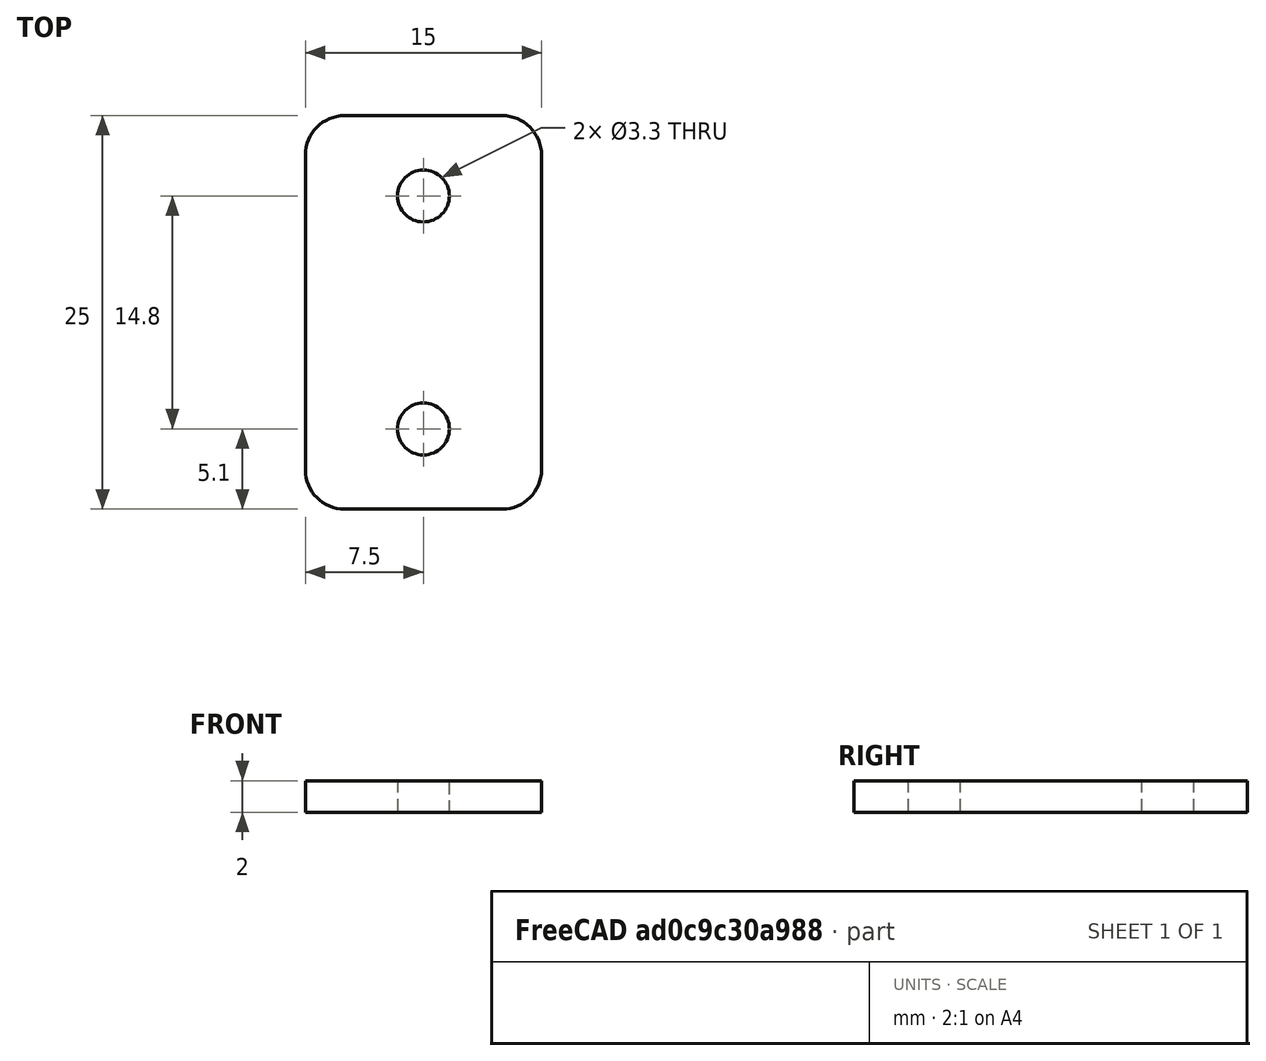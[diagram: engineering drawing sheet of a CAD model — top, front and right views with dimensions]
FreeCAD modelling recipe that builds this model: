
FCSTD DOCUMENT  (FreeCAD 1.0R39109 (Git))
Label: joint_screen
License: All rights reserved
LicenseURL: https://en.wikipedia.org/wiki/All_rights_reserved
objects: Sketcher::SketchObject×1, PartDesign::Pad×1, PartDesign::Body×1
note: 6 computed .brp shape members not serialized (recipe doc carries the construction recipe); baked Part::Feature solids carry a one-line shape summary decoded from their .brp

FEATURE [Sketcher::SketchObject] Sketch
  ArcFitTolerance = 1e-06
  AttachmentSupport = -> [XY_Plane]
  FullyConstrained = true
  MakeInternals = false
  MapMode = 5
  sketch-geometry (12):
    g0: LineSegment StartX=-7.5 StartY=10 StartZ=0 EndX=-7.5 EndY=-10 EndZ=0
    g1: LineSegment StartX=-5 StartY=-12.5 StartZ=0 EndX=5 EndY=-12.5 EndZ=0
    g2: LineSegment StartX=7.5 StartY=-10 StartZ=0 EndX=7.5 EndY=10 EndZ=0
    g3: LineSegment StartX=5 StartY=12.5 StartZ=0 EndX=-5 EndY=12.5 EndZ=0
    g4: ArcOfCircle CenterX=-5 CenterY=10 CenterZ=0 NormalX=0 NormalY=0 NormalZ=1 AngleXU=0 Radius=2.5 StartAngle=1.5708 EndAngle=3.14159
    g5: ArcOfCircle CenterX=-5 CenterY=-10 CenterZ=0 NormalX=0 NormalY=0 NormalZ=1 AngleXU=0 Radius=2.5 StartAngle=3.14159 EndAngle=4.71239
    g6: ArcOfCircle CenterX=5 CenterY=-10 CenterZ=0 NormalX=0 NormalY=0 NormalZ=1 AngleXU=0 Radius=2.5 StartAngle=4.71239 EndAngle=6.28319
    g7: ArcOfCircle CenterX=5 CenterY=10 CenterZ=0 NormalX=0 NormalY=0 NormalZ=1 AngleXU=0 Radius=2.5 StartAngle=6.92e-14 EndAngle=1.5708
    g8: GeomPoint [constr] X=-7.5 Y=12.5 Z=0
    g9: GeomPoint [constr] X=7.5 Y=-12.5 Z=0
    g10: Circle CenterX=0 CenterY=7.4 CenterZ=0 NormalX=0 NormalY=0 NormalZ=1 AngleXU=0 Radius=1.65
    g11: Circle CenterX=0 CenterY=-7.4 CenterZ=0 NormalX=0 NormalY=0 NormalZ=1 AngleXU=0 Radius=1.65
  constraints (28):
    c: Tangent(g0,g4) = -1.5708
    c: Tangent(g0,g5) = -1.5708
    c: Tangent(g1,g5) = -1.5708
    c: Tangent(g1,g6) = -1.5708
    c: Tangent(g2,g6) = -1.5708
    c: Tangent(g2,g7) = -1.5708
    c: Tangent(g3,g7) = -1.5708
    c: Tangent(g3,g4) = -1.5708
    c: Vertical(g0)
    c: Vertical(g2)
    c: Horizontal(g1)
    c: Horizontal(g3)
    c: Equal(g4,g5)
    c: Equal(g5,g6)
    c: Equal(g6,g7)
    c: PointOnObject(g8,g0)
    c: PointOnObject(g8,g3)
    c: PointOnObject(g9,g1)
    c: PointOnObject(g9,g2)
    c: Symmetric(g9,g8,g-1)
    c: DistanceX(g0,g2) = 15
    c: PointOnObject(g10,g-2)
    c: Symmetric(g11,g10,g-1)
    c: Equal(g11,g10)
    c: Radius(g11) = 1.65
    c: DistanceY(g11,g10) = 14.8
    c: DistanceY(g1,g3) = 25
    c: Radius(g7) = 2.5
FEATURE [PartDesign::Pad] Pad  label="JointBase"
  Direction = (0,0,1)
  Length = 2
  Length2 = 10
  Profile = -> Sketch
  ReferenceAxis = -> Sketch [N_Axis]
  Refine = true
  Suppressed = false
  Type = 0
FEATURE [PartDesign::Body] Body  label="joint_screen"
  AllowCompound = false
  Group = -> [Sketch,Pad]
  Origin = -> Origin
  Tip = -> Pad
